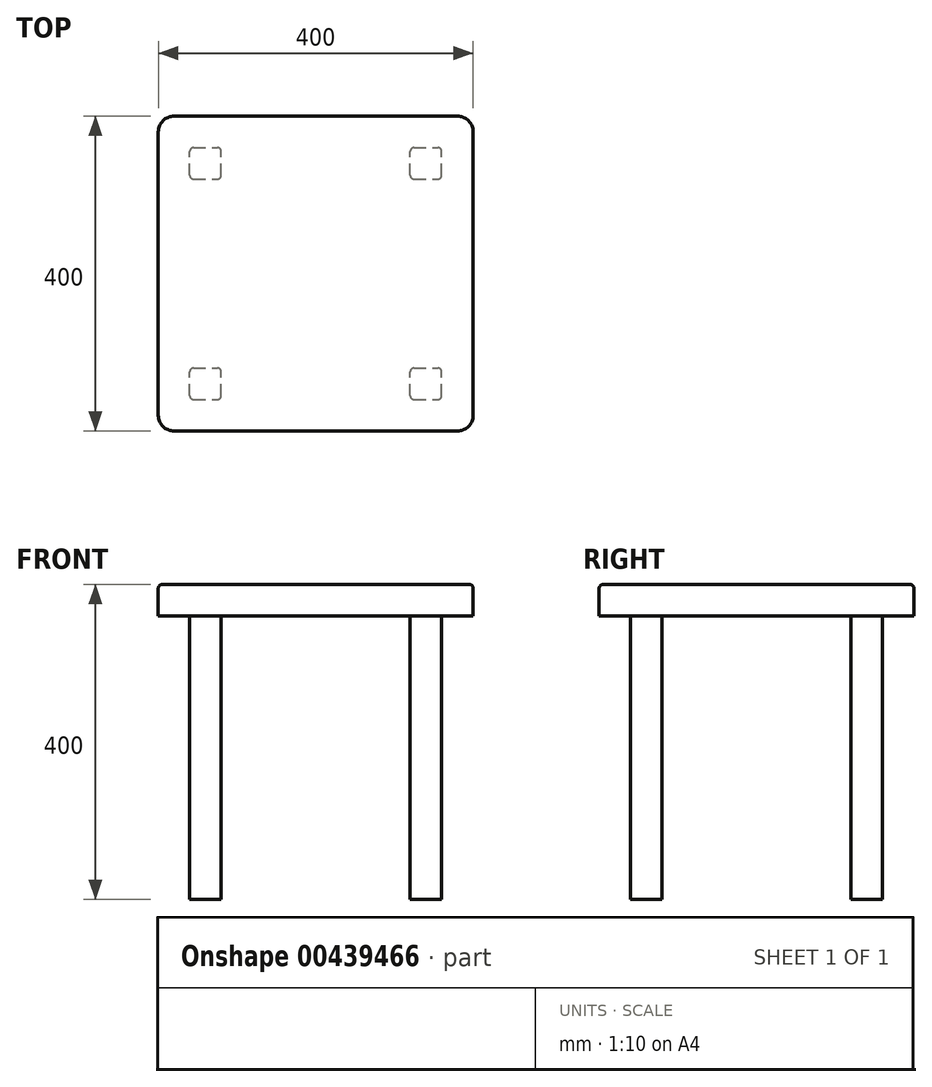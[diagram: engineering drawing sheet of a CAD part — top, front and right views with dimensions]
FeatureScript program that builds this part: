
annotation { "Feature Type Name" : "Feature", "Feature Type Description" : "" }
export const myFeature = defineFeature(function(context is Context, id is Id, definition is map)
    precondition{}
    {
        {
            var Q0;
            Q0=qCreatedBy(makeId("Top.planeOp"),FACE);
            var sketch = newSketch(context, id + "F0", { "sketchPlane" : qUnion([Q0])});
            skLineSegment(sketch, "E0.bottom", {"start": v(-180.24, 214.54) * mm, "end": v(179.76, 214.54) * mm});
            skLineSegment(sketch, "E0.top", {"start": v(-180.24, -185.46) * mm, "end": v(179.76, -185.46) * mm});
            skLineSegment(sketch, "E0.left", {"start": v(-200.24, 194.54) * mm, "end": v(-200.24, -165.46) * mm});
            skLineSegment(sketch, "E0.right", {"start": v(199.76, 194.54) * mm, "end": v(199.76, -165.46) * mm});
            skPoint(sketch, "E1.visualSharp", {"position": v(-200.24, 214.54) * mm});
            skArc(sketch, "E1.filletArc", {"start": v(-180.24, 214.54) * mm, "mid": v(-194.39, 208.68) * mm, "end": v(-200.24, 194.54) * mm});
            skPoint(sketch, "E2.visualSharp", {"position": v(199.76, 214.54) * mm});
            skArc(sketch, "E2.filletArc", {"start": v(199.76, 194.54) * mm, "mid": v(193.9, 208.68) * mm, "end": v(179.76, 214.54) * mm});
            skPoint(sketch, "E3.visualSharp", {"position": v(199.76, -185.46) * mm});
            skArc(sketch, "E3.filletArc", {"start": v(179.76, -185.46) * mm, "mid": v(193.9, -179.6) * mm, "end": v(199.76, -165.46) * mm});
            skPoint(sketch, "E4.visualSharp", {"position": v(-200.24, -185.46) * mm});
            skArc(sketch, "E4.filletArc", {"start": v(-200.24, -165.46) * mm, "mid": v(-194.39, -179.6) * mm, "end": v(-180.24, -185.46) * mm});
            skSolve(sketch);
        }
        {
            var Q0;
            Q0=makeQuery(id+"F0.imprint","IMPRINT",FACE,{"disambiguationData":[TD([[makeQuery(id+"F0.imprint","IMPRINT",EDGE,{"derivedFrom":sQuery(id+"F0.wireOp",EDGE,"E0.bottom")}),-1.0]])]});
            extrude(context, id + "F1", {"entities" : qUnion([Q0]), "depth" : 40 * mm});
        }
        {
            var Q0;
            Q0=makeQuery(id+"F1.opExtrude","CAP_FACE",FACE,{"disambiguationData":[OSD([sQuery(id+"F0.wireOp",EDGE,"E0.bottom"),sQuery(id+"F0.wireOp",EDGE,"E0.top"),sQuery(id+"F0.wireOp",EDGE,"E0.left"),sQuery(id+"F0.wireOp",EDGE,"E0.right"),sQuery(id+"F0.wireOp",EDGE,"E1.filletArc"),sQuery(id+"F0.wireOp",EDGE,"E2.filletArc"),sQuery(id+"F0.wireOp",EDGE,"E3.filletArc"),sQuery(id+"F0.wireOp",EDGE,"E4.filletArc")])],"isStart":true});
            var sketch = newSketch(context, id + "F2", { "sketchPlane" : qUnion([Q0])});
            skLineSegment(sketch, "E5.bottom", {"start": v(-155.24, 145.46) * mm, "end": v(-125.24, 145.46) * mm});
            skLineSegment(sketch, "E5.top", {"start": v(-155.24, 105.46) * mm, "end": v(-125.24, 105.46) * mm});
            skLineSegment(sketch, "E5.left", {"start": v(-160.24, 140.46) * mm, "end": v(-160.24, 110.46) * mm});
            skLineSegment(sketch, "E5.right", {"start": v(-120.24, 140.46) * mm, "end": v(-120.24, 110.46) * mm});
            skPoint(sketch, "E6.visualSharp", {"position": v(-160.24, 145.46) * mm});
            skArc(sketch, "E6.filletArc", {"start": v(-155.24, 145.46) * mm, "mid": v(-158.78, 144) * mm, "end": v(-160.24, 140.46) * mm});
            skPoint(sketch, "E7.visualSharp", {"position": v(-120.24, 145.46) * mm});
            skArc(sketch, "E7.filletArc", {"start": v(-120.24, 140.46) * mm, "mid": v(-121.7, 144) * mm, "end": v(-125.24, 145.46) * mm});
            skPoint(sketch, "E8.visualSharp", {"position": v(-120.24, 105.46) * mm});
            skArc(sketch, "E8.filletArc", {"start": v(-125.24, 105.46) * mm, "mid": v(-121.7, 106.93) * mm, "end": v(-120.24, 110.46) * mm});
            skPoint(sketch, "E9.visualSharp", {"position": v(-160.24, 105.46) * mm});
            skArc(sketch, "E9.filletArc", {"start": v(-160.24, 110.46) * mm, "mid": v(-158.78, 106.93) * mm, "end": v(-155.24, 105.46) * mm});
            skPoint(sketch, "E10.0.1.0", {"position": v(-160.24, -174.54) * mm});
            skPoint(sketch, "E10.0.1.1", {"position": v(-120.24, -134.54) * mm});
            skLineSegment(sketch, "E10.0.1.2", {"start": v(-155.24, -134.54) * mm, "end": v(-125.24, -134.54) * mm});
            skLineSegment(sketch, "E10.0.1.3", {"start": v(-155.24, -174.54) * mm, "end": v(-125.24, -174.54) * mm});
            skLineSegment(sketch, "E10.0.1.4", {"start": v(-160.24, -139.54) * mm, "end": v(-160.24, -169.54) * mm});
            skLineSegment(sketch, "E10.0.1.5", {"start": v(-120.24, -139.54) * mm, "end": v(-120.24, -169.54) * mm});
            skPoint(sketch, "E10.0.1.6", {"position": v(-120.24, -174.54) * mm});
            skPoint(sketch, "E10.0.1.7", {"position": v(-160.24, -134.54) * mm});
            skArc(sketch, "E10.0.1.8", {"start": v(-125.24, -174.54) * mm, "mid": v(-121.7, -173.07) * mm, "end": v(-120.24, -169.54) * mm});
            skArc(sketch, "E10.0.1.9", {"start": v(-160.24, -169.54) * mm, "mid": v(-158.78, -173.07) * mm, "end": v(-155.24, -174.54) * mm});
            skArc(sketch, "E10.0.1.10", {"start": v(-155.24, -134.54) * mm, "mid": v(-158.78, -136) * mm, "end": v(-160.24, -139.54) * mm});
            skArc(sketch, "E10.0.1.11", {"start": v(-120.24, -139.54) * mm, "mid": v(-121.7, -136) * mm, "end": v(-125.24, -134.54) * mm});
            skPoint(sketch, "E10.1.0.0", {"position": v(119.76, 105.46) * mm});
            skPoint(sketch, "E10.1.0.1", {"position": v(159.76, 145.46) * mm});
            skLineSegment(sketch, "E10.1.0.2", {"start": v(124.76, 145.46) * mm, "end": v(154.76, 145.46) * mm});
            skLineSegment(sketch, "E10.1.0.3", {"start": v(124.76, 105.46) * mm, "end": v(154.76, 105.46) * mm});
            skLineSegment(sketch, "E10.1.0.4", {"start": v(119.76, 140.46) * mm, "end": v(119.76, 110.46) * mm});
            skLineSegment(sketch, "E10.1.0.5", {"start": v(159.76, 140.46) * mm, "end": v(159.76, 110.46) * mm});
            skPoint(sketch, "E10.1.0.6", {"position": v(159.76, 105.46) * mm});
            skPoint(sketch, "E10.1.0.7", {"position": v(119.76, 145.46) * mm});
            skArc(sketch, "E10.1.0.8", {"start": v(154.76, 105.46) * mm, "mid": v(158.3, 106.93) * mm, "end": v(159.76, 110.46) * mm});
            skArc(sketch, "E10.1.0.9", {"start": v(119.76, 110.46) * mm, "mid": v(121.22, 106.93) * mm, "end": v(124.76, 105.46) * mm});
            skArc(sketch, "E10.1.0.10", {"start": v(124.76, 145.46) * mm, "mid": v(121.22, 144) * mm, "end": v(119.76, 140.46) * mm});
            skArc(sketch, "E10.1.0.11", {"start": v(159.76, 140.46) * mm, "mid": v(158.3, 144) * mm, "end": v(154.76, 145.46) * mm});
            skPoint(sketch, "E10.1.1.0", {"position": v(119.76, -174.54) * mm});
            skPoint(sketch, "E10.1.1.1", {"position": v(159.76, -134.54) * mm});
            skLineSegment(sketch, "E10.1.1.2", {"start": v(124.76, -134.54) * mm, "end": v(154.76, -134.54) * mm});
            skLineSegment(sketch, "E10.1.1.3", {"start": v(124.76, -174.54) * mm, "end": v(154.76, -174.54) * mm});
            skLineSegment(sketch, "E10.1.1.4", {"start": v(119.76, -139.54) * mm, "end": v(119.76, -169.54) * mm});
            skLineSegment(sketch, "E10.1.1.5", {"start": v(159.76, -139.54) * mm, "end": v(159.76, -169.54) * mm});
            skPoint(sketch, "E10.1.1.6", {"position": v(159.76, -174.54) * mm});
            skPoint(sketch, "E10.1.1.7", {"position": v(119.76, -134.54) * mm});
            skArc(sketch, "E10.1.1.8", {"start": v(154.76, -174.54) * mm, "mid": v(158.3, -173.07) * mm, "end": v(159.76, -169.54) * mm});
            skArc(sketch, "E10.1.1.9", {"start": v(119.76, -169.54) * mm, "mid": v(121.22, -173.07) * mm, "end": v(124.76, -174.54) * mm});
            skArc(sketch, "E10.1.1.10", {"start": v(124.76, -134.54) * mm, "mid": v(121.22, -136) * mm, "end": v(119.76, -139.54) * mm});
            skArc(sketch, "E10.1.1.11", {"start": v(159.76, -139.54) * mm, "mid": v(158.3, -136) * mm, "end": v(154.76, -134.54) * mm});
            skLineSegment(sketch, "E10.direction1", {"start": v(-160.24, 105.46) * mm, "end": v(119.76, 105.46) * mm, "construction": true});
            skLineSegment(sketch, "E10.direction2", {"start": v(-160.24, 105.46) * mm, "end": v(-160.24, -174.54) * mm, "construction": true});
            skSolve(sketch);
        }
        {
            var Q0;
            Q0=makeQuery(id+"F2.imprint","IMPRINT",FACE,{"disambiguationData":[TD([[makeQuery(id+"F2.imprint","IMPRINT",EDGE,{"derivedFrom":sQuery(id+"F2.wireOp",EDGE,"E5.bottom")}),-1.0]])]});
            var Q1;
            Q1=makeQuery(id+"F2.imprint","IMPRINT",FACE,{"disambiguationData":[TD([[makeQuery(id+"F2.imprint","IMPRINT",EDGE,{"derivedFrom":sQuery(id+"F2.wireOp",EDGE,"E10.0.1.2")}),-1.0]])]});
            var Q2;
            Q2=makeQuery(id+"F2.imprint","IMPRINT",FACE,{"disambiguationData":[TD([[makeQuery(id+"F2.imprint","IMPRINT",EDGE,{"derivedFrom":sQuery(id+"F2.wireOp",EDGE,"E10.1.1.2")}),-1.0]])]});
            var Q3;
            Q3=makeQuery(id+"F2.imprint","IMPRINT",FACE,{"disambiguationData":[TD([[makeQuery(id+"F2.imprint","IMPRINT",EDGE,{"derivedFrom":sQuery(id+"F2.wireOp",EDGE,"E10.1.0.2")}),-1.0]])]});
            extrude(context, id + "F3", {"entities" : qUnion([Q0, Q1, Q2, Q3]), "operationType" : NewBodyOperationType.ADD, "depth" : 360 * mm});
        }
        {
            var Q0;
            Q0=makeQuery(id+"F1.opExtrude","CAP_FACE",FACE,{"disambiguationData":[OSD([sQuery(id+"F0.wireOp",EDGE,"E0.bottom"),sQuery(id+"F0.wireOp",EDGE,"E0.top"),sQuery(id+"F0.wireOp",EDGE,"E0.left"),sQuery(id+"F0.wireOp",EDGE,"E0.right"),sQuery(id+"F0.wireOp",EDGE,"E1.filletArc"),sQuery(id+"F0.wireOp",EDGE,"E2.filletArc"),sQuery(id+"F0.wireOp",EDGE,"E3.filletArc"),sQuery(id+"F0.wireOp",EDGE,"E4.filletArc")])],"isStart":false});
            fillet(context, id + "F4", {"entities" : qUnion([Q0]), "radius" : 5 * mm, "tangentPropagation" : true, "allowEdgeOverflow" : false});
        }
    });
